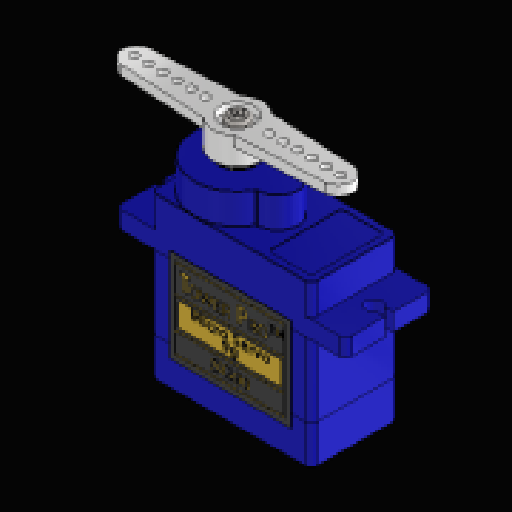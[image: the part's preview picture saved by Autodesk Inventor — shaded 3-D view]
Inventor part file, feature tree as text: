
AUTODESK INVENTOR PART (.ipt)
format: ipt  version: 2023.2 (Build 272271030, 271C)  size: 1,929,728 bytes
history: mixed  units: mm
features: other x18, extrude x1, sketch x1, projected_geometry x1, imported_body x1
ambient origin geometry x8: Origin, YZ Plane, XZ Plane, XY Plane, X Axis, Y Axis, Z Axis, Center Point
bodies: Solid1 (imported_parasolid), Solid2 (imported_parasolid), Solid3 (imported_parasolid), Solid4 (imported_parasolid), Solid5 (imported_parasolid), Solid6 (imported_parasolid), Solid7 (imported_parasolid), Solid8 (imported_parasolid), Solid9 (imported_parasolid), Solid10 (imported_parasolid), Solid11 (imported_parasolid), Solid12 (imported_parasolid), Solid13 (imported_parasolid), Solid14 (imported_parasolid), Solid17 (imported_parasolid)
feature tree (22):
  other  "Plane4"
  other  "Plane4:1"
  other  "Plane4:2"
  extrude  "Extrusion1"  Depth=10.0mm
  sketch  "Sketch2"  dims[d7=23.0mm d8=2.0mm d9=2.0mm d10=10.0mm d11=0.0mm]
  projected_geometry  "Projected Loop1"
  other  "Tower Pro - Micro Servo 9g - SG90.1:1"
  other  "Tower Pro - Micro Servo 9g - SG90.1:2"
  other  "Tower Pro - Micro Servo 9g - SG90.1:3"
  other  "Tower Pro - Micro Servo 9g - SG90.1:4"
  other  "Tower Pro - Micro Servo 9g - SG90.1:5"
  other  "Tower Pro - Micro Servo 9g - SG90.1:6"
  other  "Tower Pro - Micro Servo 9g - SG90.1:7"
  other  "Tower Pro - Micro Servo 9g - SG90.1:8"
  other  "Tower Pro - Micro Servo 9g - SG90.1:9"
  other  "Tower Pro - Micro Servo 9g - SG90.1:10"
  other  "Tower Pro - Micro Servo 9g - SG90.1:11"
  other  "Tower Pro - Micro Servo 9g - SG90.1:12"
  other  "Tower Pro - Micro Servo 9g - SG90.1:13"
  other  "SG90 - Micro Servo 9g - Tower Pro.3:1"
  other  "SG90 - Micro Servo 9g - Tower Pro.6:1"
  imported_body  NMx_Import_Brep_tag  [imported B-rep: ~76 faces, bbox_mm=[18.75, 10.3, 12.4]]
